# Revit family: RRTNTCT304
name_source: partatom
category: Generic Models
revit_build: Autodesk Revit 2018 (Build: 20190510_1515(x64)
units: mm (PartAtom-declared; Revit-internal decimal feet)

## family parameters
Always vertical = No
Can host rebar = No
Cut with Voids When Loaded = No
Part Type = Normal
Room Calculation Point = No
Round Connector Dimension = Use Diameter
Shared = Yes
Work Plane-Based = Yes

## types (4) — shared parameters
Arm Height = 2 "
Arm Material = <By Category>
Default Elevation = 48 "

## per-type parameters (varying)
| type | Arm Length | Arm Offset | Arm Type | Description |
| RRTNTCT30418 | 18 " | 9.245 " | RMTNT304MOD : RMTNT304MOD18 | Post Tented Cantilever Rack for Post Mount 304 18 Inch long |
| RRTNTCT30424 | 24 " | 12.245 " | RMTNT304MOD : RMTNT304MOD24 | Post Tented Cantilever Rack for Post Mount 304 24 Inch long |
| RRTNTCT30430 | 30 " | 15.245 " | RMTNT304MOD : RMTNT304MOD30 | Post Tented Cantilever Rack for Post Mount 304 30 Inch long |
| RRTNTCT30412 | 12 " | 6.245 " | RMTNT304MOD : RMTNT304MOD12 | Post Tented Cantilever Rack for Post Mount 304 12 Inch long |

note: column(s) folded — value = type name in every type: Catalog Number

## geometry (parser evidence)
native form markers: Sweep x18
no freeform markers — native parametric forms only
